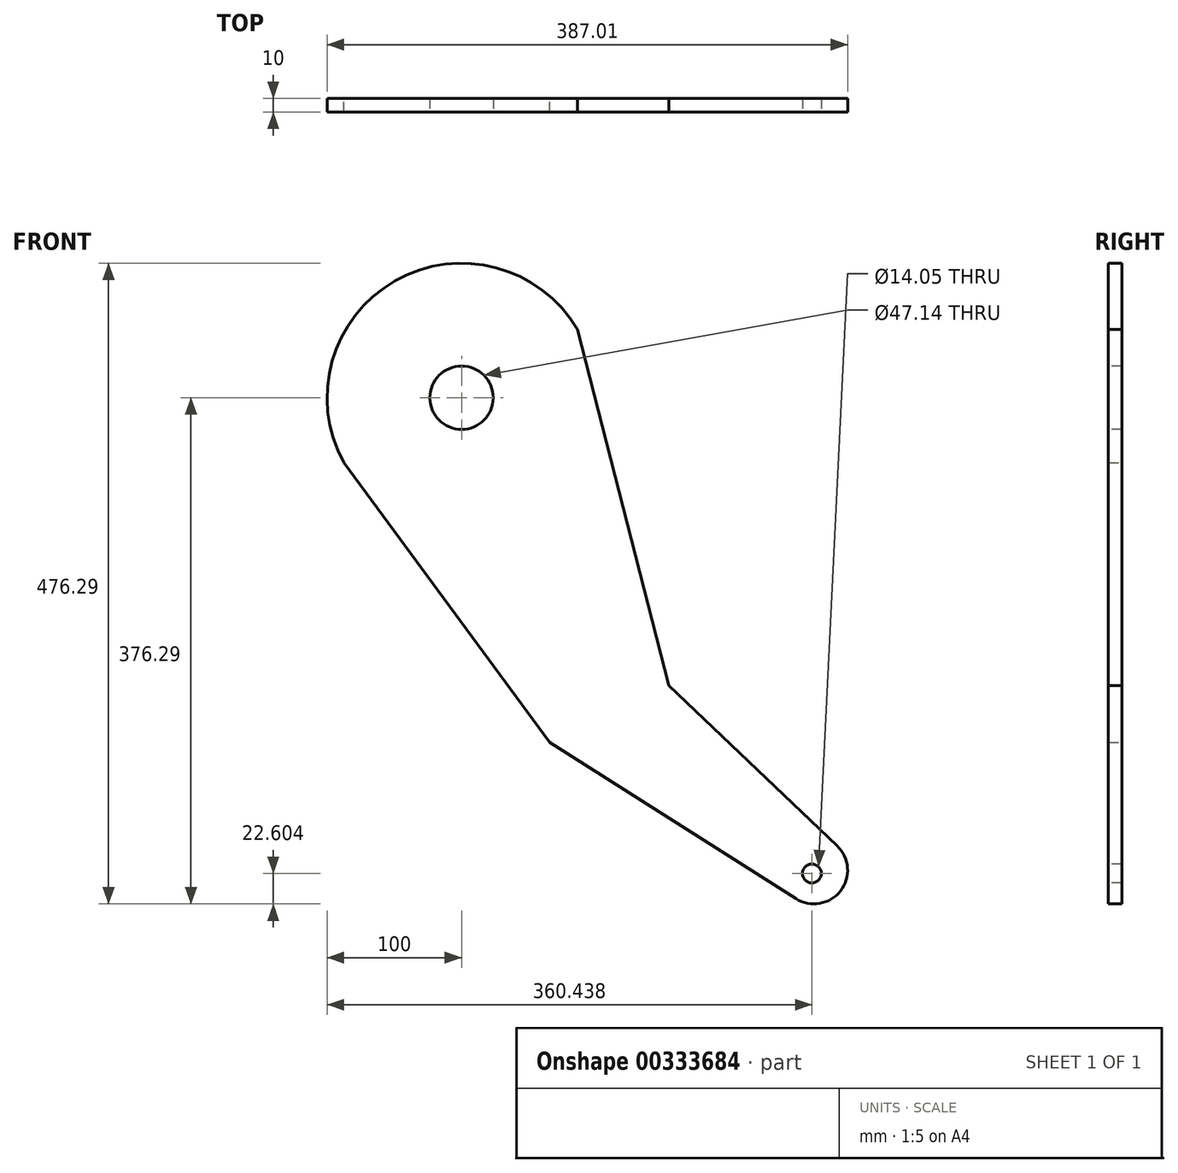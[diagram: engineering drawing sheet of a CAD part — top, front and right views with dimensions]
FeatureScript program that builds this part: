
annotation { "Feature Type Name" : "Feature", "Feature Type Description" : "" }
export const myFeature = defineFeature(function(context is Context, id is Id, definition is map)
    precondition{}
    {
        {
            var Q0;
            Q0=qCreatedBy(makeId("Front.planeOp"),FACE);
            var sketch = newSketch(context, id + "F0", { "sketchPlane" : qUnion([Q0])});
            skArc(sketch, "E0", {"start": v(86.14, 50.79) * mm, "mid": v(-49.55, 86.86) * mm, "end": v(-87.56, -48.3) * mm});
            skLineSegment(sketch, "E1", {"start": v(0, 0) * mm, "end": v(0, -172.59) * mm, "construction": true});
            skLineSegment(sketch, "E2", {"start": v(0, -172.59) * mm, "end": v(0, -213.3) * mm, "construction": true});
            skLineSegment(sketch, "E3", {"start": v(105.65, -226.58) * mm, "end": v(111.91, -478.7) * mm, "construction": true});
            skArc(sketch, "E4", {"start": v(248.62, -372.4) * mm, "mid": v(281.71, -366.68) * mm, "end": v(279.23, -333.18) * mm});
            skLineSegment(sketch, "E5", {"start": v(-87.56, -48.3) * mm, "end": v(65.38, -256.2) * mm});
            skLineSegment(sketch, "E6", {"start": v(65.38, -256.2) * mm, "end": v(248.62, -372.4) * mm});
            skLineSegment(sketch, "E7", {"start": v(86.14, 50.79) * mm, "end": v(154.09, -214.16) * mm});
            skLineSegment(sketch, "E8", {"start": v(154.09, -214.16) * mm, "end": v(279.23, -333.18) * mm});
            skSolve(sketch);
        }
        {
            var Q0;
            Q0 = qSketchRegion(id + "F0", true);
            extrude(context, id + "F1", {"entities" : qUnion([Q0]), "depth" : 10 * mm});
        }
        {
            var Q0;
            Q0=makeQuery(id+"F1.opExtrude","CAP_FACE",FACE,{"disambiguationData":[OSD([sQuery(id+"F0.wireOp",EDGE,"E0"),sQuery(id+"F0.wireOp",EDGE,"E4"),sQuery(id+"F0.wireOp",EDGE,"E5"),sQuery(id+"F0.wireOp",EDGE,"E6"),sQuery(id+"F0.wireOp",EDGE,"E7"),sQuery(id+"F0.wireOp",EDGE,"E8")])],"isStart":false});
            var sketch = newSketch(context, id + "F2", { "sketchPlane" : qUnion([Q0])});
            skSolve(sketch);
        }
        {
            var Q0;
            Q0=makeQuery(id+"F2.imprint","IMPRINT",FACE,{"disambiguationData":[TD([[makeQuery(id+"F2.imprint","IMPRINT",EDGE,{"derivedFrom":makeQuery(id+"F1.opExtrude","CAP_EDGE",EDGE,{"disambiguationData":[OSD([sQuery(id+"F0.wireOp",EDGE,"E0")])],"isStart":false})}),1.0]])]});
            var sketch = newSketch(context, id + "F3", { "sketchPlane" : qUnion([Q0])});
            skCircle(sketch, "E9", {"center": v(0, 0) * mm, "radius": 23.57 * mm});
            skCircle(sketch, "E10", {"center": v(260.44, -353.69) * mm, "radius": 7.02 * mm});
            skSolve(sketch);
        }
        {
            var Q0;
            Q0 = qSketchRegion(id + "F3", true);
            extrude(context, id + "F4", {"entities" : qUnion([Q0]), "operationType" : NewBodyOperationType.REMOVE, "oppositeDirection" : true, "depth" : 71.12 * mm});
        }
    });
